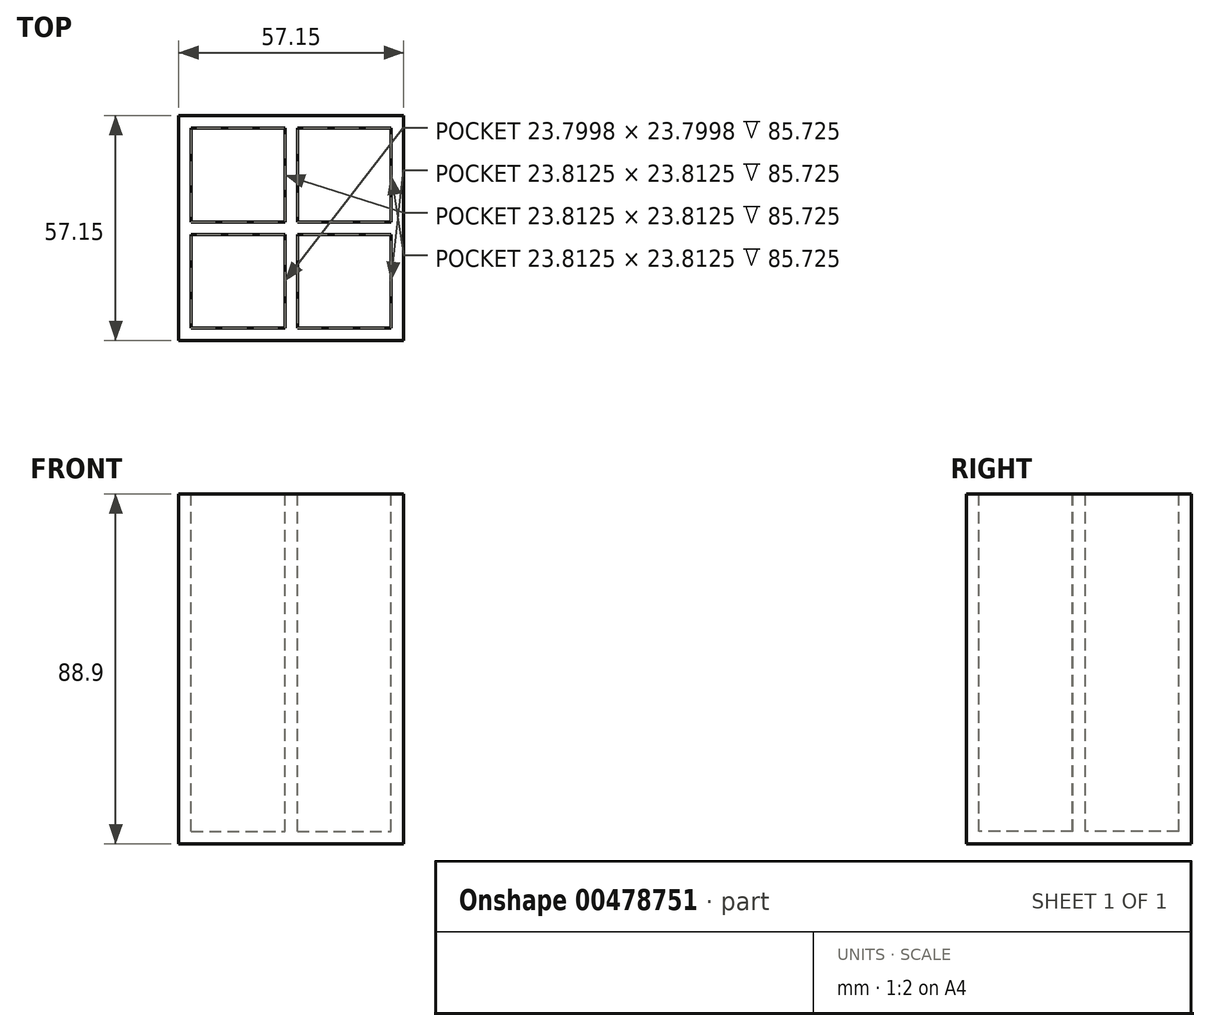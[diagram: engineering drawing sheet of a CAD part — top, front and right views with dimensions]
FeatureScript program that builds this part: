
annotation { "Feature Type Name" : "Feature", "Feature Type Description" : "" }
export const myFeature = defineFeature(function(context is Context, id is Id, definition is map)
    precondition{}
    {
        {
            var Q0;
            Q0=qCreatedBy(makeId("Front.planeOp"),FACE);
            var sketch = newSketch(context, id + "F0", { "sketchPlane" : qUnion([Q0])});
            skLineSegment(sketch, "E0.bottom", {"start": v(-39.6, 66.35) * mm, "end": v(17.55, 66.35) * mm});
            skLineSegment(sketch, "E0.top", {"start": v(-39.6, -22.55) * mm, "end": v(17.55, -22.55) * mm});
            skLineSegment(sketch, "E0.left", {"start": v(-39.6, 66.35) * mm, "end": v(-39.6, -22.55) * mm});
            skLineSegment(sketch, "E0.right", {"start": v(17.55, 66.35) * mm, "end": v(17.55, -22.55) * mm});
            skSolve(sketch);
        }
        {
            var Q0;
            Q0=makeQuery(id+"F0.imprint","IMPRINT",FACE,{"disambiguationData":[TD([[makeQuery(id+"F0.imprint","IMPRINT",EDGE,{"derivedFrom":sQuery(id+"F0.wireOp",EDGE,"E0.bottom")}),-1.0]])]});
            extrude(context, id + "F1", {"entities" : qUnion([Q0]), "depth" : 57.15 * mm});
        }
        {
            var Q0;
            Q0=makeQuery(id+"F1.opExtrude","SWEPT_FACE",FACE,{"disambiguationData":[OSD([sQuery(id+"F0.wireOp",EDGE,"E0.bottom")])]});
            var sketch = newSketch(context, id + "F2", { "sketchPlane" : qUnion([Q0])});
            skSolve(sketch);
        }
        {
            var Q0;
            {var subQ0=sQuery(id+"F0.wireOp",EDGE,"E0.bottom");Q0=makeQuery(id+"F2.imprint","IMPRINT",FACE,{"disambiguationData":[TD([[makeQuery(id+"F2.imprint","IMPRINT",EDGE,{"derivedFrom":makeQuery(id+"F1.opExtrude","CAP_EDGE",EDGE,{"disambiguationData":[OSD([subQ0])],"isStart":true})}),-1.0]])]});}
            var sketch = newSketch(context, id + "F3", { "sketchPlane" : qUnion([Q0])});
            skLineSegment(sketch, "E1.bottom", {"start": v(-36.43, -30.18) * mm, "end": v(-12.63, -30.18) * mm});
            skLineSegment(sketch, "E1.top", {"start": v(-36.43, -53.98) * mm, "end": v(-12.63, -53.98) * mm});
            skLineSegment(sketch, "E1.left", {"start": v(-36.43, -30.18) * mm, "end": v(-36.43, -53.98) * mm});
            skLineSegment(sketch, "E1.right", {"start": v(-12.63, -30.18) * mm, "end": v(-12.63, -53.98) * mm});
            skSolve(sketch);
        }
        {
            var Q0;
            Q0=makeQuery(id+"F3.imprint","IMPRINT",FACE,{"disambiguationData":[TD([[makeQuery(id+"F3.imprint","IMPRINT",EDGE,{"derivedFrom":sQuery(id+"F3.wireOp",EDGE,"E1.bottom")}),-1.0]])]});
            extrude(context, id + "F4", {"entities" : qUnion([Q0]), "operationType" : NewBodyOperationType.REMOVE, "oppositeDirection" : true, "depth" : 85.72 * mm});
        }
        {
            var Q0;
            {var subQ0=sQuery(id+"F0.wireOp",EDGE,"E0.bottom");Q0=makeQuery(id+"F2.imprint","IMPRINT",FACE,{"disambiguationData":[TD([[makeQuery(id+"F2.imprint","IMPRINT",EDGE,{"derivedFrom":makeQuery(id+"F1.opExtrude","CAP_EDGE",EDGE,{"disambiguationData":[OSD([subQ0])],"isStart":true})}),-1.0]])]});}
            var sketch = newSketch(context, id + "F5", { "sketchPlane" : qUnion([Q0])});
            skLineSegment(sketch, "E2.bottom", {"start": v(-9.44, -30.16) * mm, "end": v(14.37, -30.16) * mm});
            skLineSegment(sketch, "E2.top", {"start": v(-9.44, -53.98) * mm, "end": v(14.37, -53.98) * mm});
            skLineSegment(sketch, "E2.left", {"start": v(-9.44, -30.16) * mm, "end": v(-9.44, -53.98) * mm});
            skLineSegment(sketch, "E2.right", {"start": v(14.37, -30.16) * mm, "end": v(14.37, -53.98) * mm});
            skSolve(sketch);
        }
        {
            var Q0;
            Q0=makeQuery(id+"F5.imprint","IMPRINT",FACE,{"disambiguationData":[TD([[makeQuery(id+"F5.imprint","IMPRINT",EDGE,{"derivedFrom":sQuery(id+"F5.wireOp",EDGE,"E2.bottom")}),-1.0]])]});
            extrude(context, id + "F6", {"entities" : qUnion([Q0]), "operationType" : NewBodyOperationType.REMOVE, "oppositeDirection" : true, "depth" : 85.72 * mm});
        }
        {
            var Q0;
            {var subQ0=sQuery(id+"F0.wireOp",EDGE,"E0.bottom");Q0=makeQuery(id+"F2.imprint","IMPRINT",FACE,{"disambiguationData":[TD([[makeQuery(id+"F2.imprint","IMPRINT",EDGE,{"derivedFrom":makeQuery(id+"F1.opExtrude","CAP_EDGE",EDGE,{"disambiguationData":[OSD([subQ0])],"isStart":true})}),-1.0]])]});}
            var sketch = newSketch(context, id + "F7", { "sketchPlane" : qUnion([Q0])});
            skLineSegment(sketch, "E3.bottom", {"start": v(-36.43, -3.18) * mm, "end": v(-12.62, -3.18) * mm});
            skLineSegment(sketch, "E3.top", {"start": v(-36.43, -26.99) * mm, "end": v(-12.62, -26.99) * mm});
            skLineSegment(sketch, "E3.left", {"start": v(-36.43, -3.18) * mm, "end": v(-36.43, -26.99) * mm});
            skLineSegment(sketch, "E3.right", {"start": v(-12.62, -3.17) * mm, "end": v(-12.62, -26.99) * mm});
            skSolve(sketch);
        }
        {
            var Q0;
            Q0=makeQuery(id+"F7.imprint","IMPRINT",FACE,{"disambiguationData":[TD([[makeQuery(id+"F7.imprint","IMPRINT",EDGE,{"derivedFrom":sQuery(id+"F7.wireOp",EDGE,"E3.bottom")}),-1.0]])]});
            extrude(context, id + "F8", {"entities" : qUnion([Q0]), "operationType" : NewBodyOperationType.REMOVE, "oppositeDirection" : true, "depth" : 85.72 * mm});
        }
        {
            var Q0;
            {var subQ0=sQuery(id+"F0.wireOp",EDGE,"E0.bottom");Q0=makeQuery(id+"F2.imprint","IMPRINT",FACE,{"disambiguationData":[TD([[makeQuery(id+"F2.imprint","IMPRINT",EDGE,{"derivedFrom":makeQuery(id+"F1.opExtrude","CAP_EDGE",EDGE,{"disambiguationData":[OSD([subQ0])],"isStart":true})}),-1.0]])]});}
            var sketch = newSketch(context, id + "F9", { "sketchPlane" : qUnion([Q0])});
            skLineSegment(sketch, "E4.bottom", {"start": v(-9.44, -3.18) * mm, "end": v(14.37, -3.18) * mm});
            skLineSegment(sketch, "E4.top", {"start": v(-9.44, -26.99) * mm, "end": v(14.37, -26.99) * mm});
            skLineSegment(sketch, "E4.left", {"start": v(-9.44, -3.18) * mm, "end": v(-9.44, -26.99) * mm});
            skLineSegment(sketch, "E4.right", {"start": v(14.37, -3.17) * mm, "end": v(14.37, -26.99) * mm});
            skSolve(sketch);
        }
        {
            var Q0;
            Q0=makeQuery(id+"F9.imprint","IMPRINT",FACE,{"disambiguationData":[TD([[makeQuery(id+"F9.imprint","IMPRINT",EDGE,{"derivedFrom":sQuery(id+"F9.wireOp",EDGE,"E4.bottom")}),-1.0]])]});
            extrude(context, id + "F10", {"entities" : qUnion([Q0]), "operationType" : NewBodyOperationType.REMOVE, "oppositeDirection" : true, "depth" : 85.72 * mm});
        }
    });
